# Revit family: P191568KX-072c_KOSC504E
name_source: partatom
category: Specialty Equipment
units: mm (PartAtom-declared; Revit-internal decimal feet)

## family parameters
Always vertical = Yes
Cut with Voids When Loaded = No
Enable Cutting in Views = No
Maintain Annotation Orientation = No
Part Type = Normal
Room Calculation Point = No
Round Connector Dimension = Use Diameter
Shared = No
Work Plane-Based = No

## types (1)
- KOSC504ESS
    Amps = 40 A
    Body Material = ARCAT - Metal - Steel - Stainless
    Clearance Material = ARCAT - Clearance
    Default Elevation = 0"
    Depth = 25 3/4"
    Description = 24" Single Wall Oven with True Convection
Four encastré simple de 24 po à convection véritable
    Dimension Guide = http://access.whirlpool.com Guide&sku=KOSC504ESS&language=EN
http://access.whirlpool.com Guide&sku=KOSC504ESS&language=EN
    Display Panel Material = ARCAT - Glass - Black
    Door Material = ARCAT - Metal - Steel - Stainless
    Family Name = COOKING
    Feature 1 = True Convection Oven
Four à convection véritable
    Feature 2 = Professionally-Inspired Design
Conception d'inspiration professionnelle
    Feature 3 = Even-Heat™ Preheat
Préchauffage Even-Heat™
    Glass Material = ARCAT - Glass - Tempered - Black
    Handle Material = ARCAT - Metal - Steel - Gray
    Height = 29"
    Installation-Fabrication = http://access.whirlpool.com Instruction&sku=KOSC504ESS&language=EN
http://access.whirlpool.com Instruction&sku=KOSC504ESS&language=FR
    Manufacturer = KitchenAid
    Model = KOSC504ESS
    Voltage = 0 V
    Width = 23 3/4"

## geometry (parser evidence)
native form markers: Sweep x5
no freeform markers — native parametric forms only
